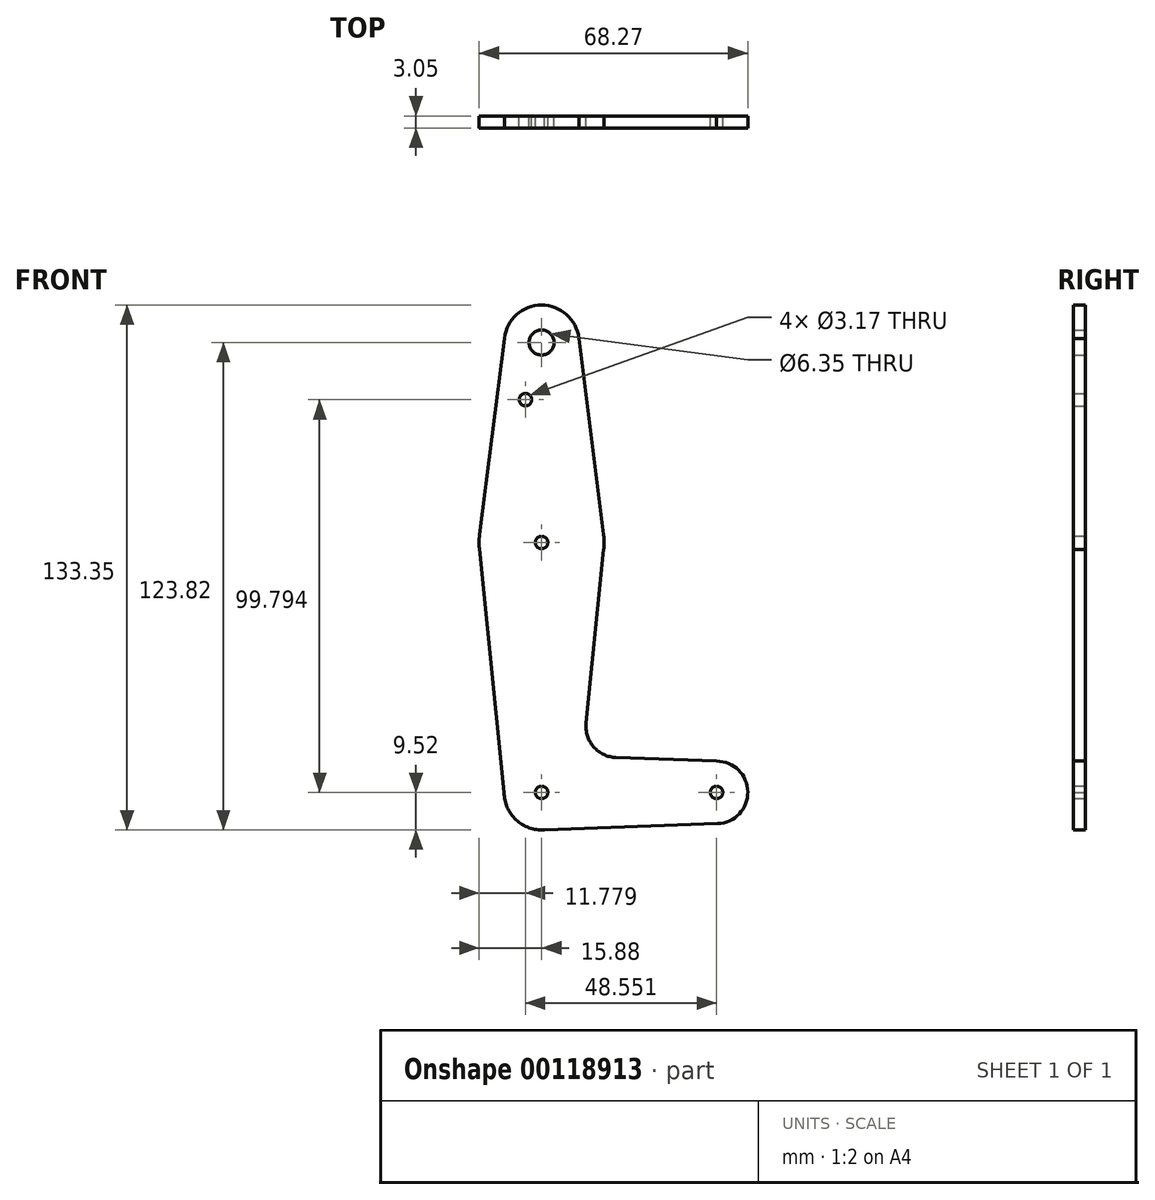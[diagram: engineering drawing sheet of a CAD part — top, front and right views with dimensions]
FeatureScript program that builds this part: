
annotation { "Feature Type Name" : "Feature", "Feature Type Description" : "" }
export const myFeature = defineFeature(function(context is Context, id is Id, definition is map)
    precondition{}
    {
        {
            var Q0;
            Q0=qCreatedBy(makeId("Front.planeOp"),FACE);
            var sketch = newSketch(context, id + "F0", { "sketchPlane" : qUnion([Q0])});
            skCircle(sketch, "E0", {"center": v(0, 68.21) * mm, "radius": 9.53 * mm});
            skCircle(sketch, "E1", {"center": v(0, -46.09) * mm, "radius": 9.53 * mm});
            skCircle(sketch, "E2", {"center": v(44.45, -46.09) * mm, "radius": 7.94 * mm});
            skCircle(sketch, "E3", {"center": v(0, 17.41) * mm, "radius": 15.88 * mm});
            skLineSegment(sketch, "E4", {"start": v(9.46, 69.28) * mm, "end": v(15.75, 19.4) * mm});
            skLineSegment(sketch, "E5", {"start": v(15.82, 16.04) * mm, "end": v(11.3, -28.5) * mm});
            skLineSegment(sketch, "E6", {"start": v(0, -55.61) * mm, "end": v(44.73, -54.02) * mm});
            skLineSegment(sketch, "E7", {"start": v(44.45, -38.15) * mm, "end": v(18.93, -37.24) * mm});
            skLineSegment(sketch, "E8", {"start": v(-9.52, -46.09) * mm, "end": v(-15.82, 16.04) * mm});
            skLineSegment(sketch, "E9", {"start": v(-15.75, 19.4) * mm, "end": v(-9.46, 69.28) * mm});
            skCircle(sketch, "E10", {"center": v(0, 17.41) * mm, "radius": 1.59 * mm});
            skCircle(sketch, "E11", {"center": v(-4.1, 53.7) * mm, "radius": 1.59 * mm});
            skPoint(sketch, "E12.newPointA", {"position": v(9.53, -46.09) * mm});
            skPoint(sketch, "E12.newPointB", {"position": v(0, -36.56) * mm});
            skArc(sketch, "E12.filletArc", {"start": v(11.3, -28.5) * mm, "mid": v(13.22, -34.52) * mm, "end": v(18.93, -37.24) * mm});
            skCircle(sketch, "E13", {"center": v(0, -46.09) * mm, "radius": 1.59 * mm});
            skCircle(sketch, "E14", {"center": v(44.45, -46.09) * mm, "radius": 1.59 * mm});
            skCircle(sketch, "E15", {"center": v(0, 68.21) * mm, "radius": 3.18 * mm});
            skSolve(sketch);
        }
        {
            var Q0;
            Q0 = qSketchRegion(id + "F0", true);
            extrude(context, id + "F1", {"entities" : qUnion([Q0]), "depth" : 3.05 * mm});
        }
    });
